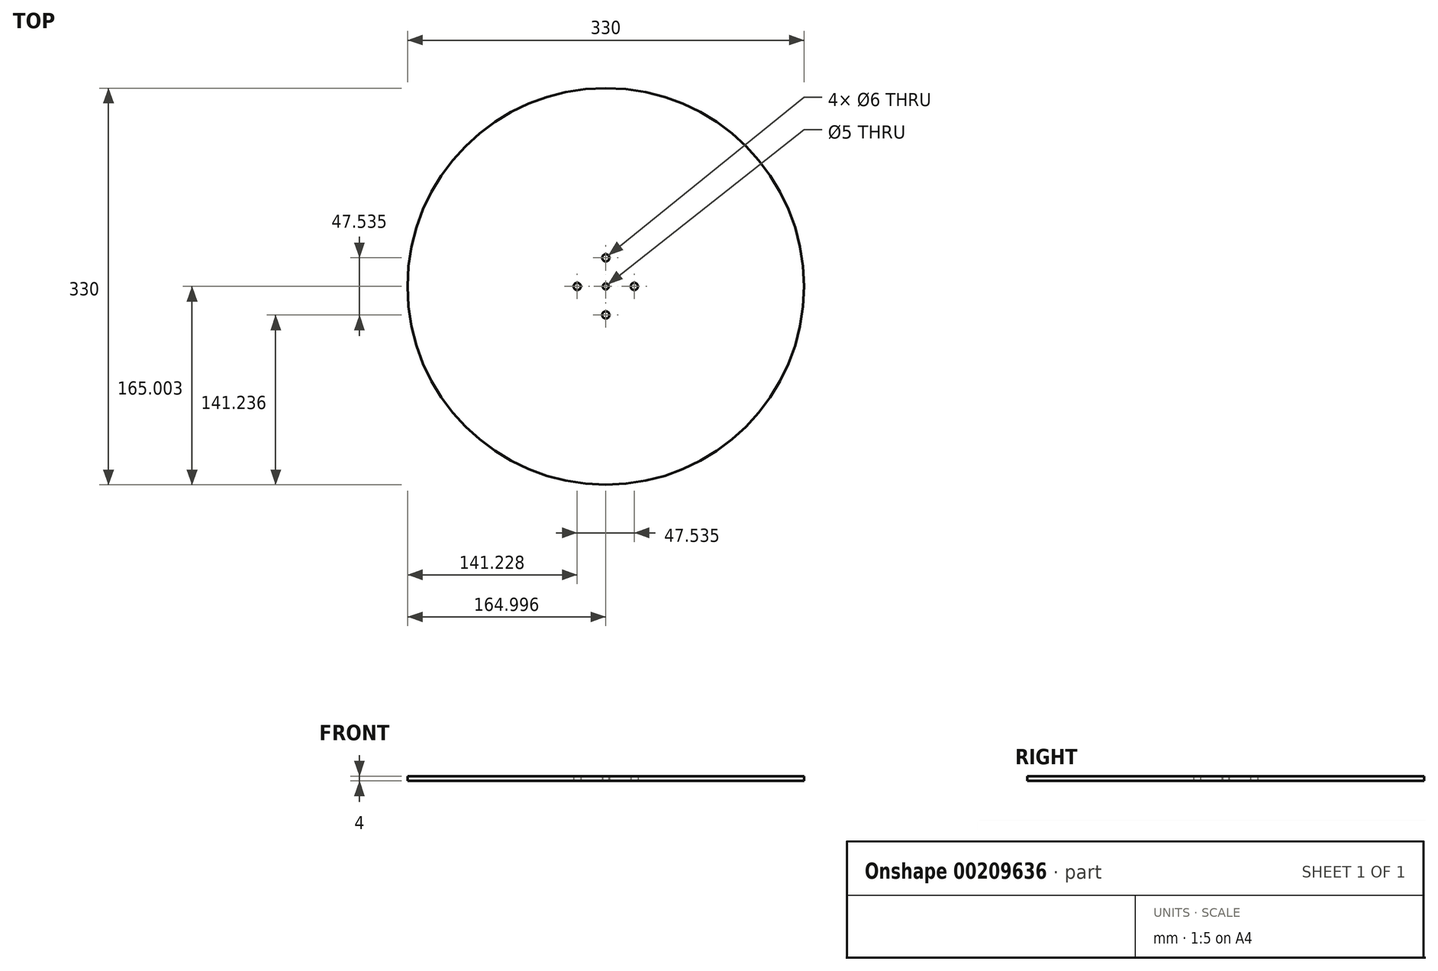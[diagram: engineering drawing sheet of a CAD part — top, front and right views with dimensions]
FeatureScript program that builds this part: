
annotation { "Feature Type Name" : "Feature", "Feature Type Description" : "" }
export const myFeature = defineFeature(function(context is Context, id is Id, definition is map)
    precondition{}
    {
        {
            var Q0;
            Q0=qCreatedBy(makeId("Top.planeOp"),FACE);
            var sketch = newSketch(context, id + "F0", { "sketchPlane" : qUnion([Q0])});
            skCircle(sketch, "E0", {"center": v(140.1, 209.35) * mm, "radius": 2.5 * mm});
            skCircle(sketch, "E1", {"center": v(140.1, 209.35) * mm, "radius": 165 * mm});
            skCircle(sketch, "E2", {"center": v(140.1, 209.35) * mm, "radius": 23.77 * mm, "construction": true});
            skCircle(sketch, "E3", {"center": v(140.1, 233.12) * mm, "radius": 3 * mm});
            skCircle(sketch, "E4", {"center": v(163.86, 209.35) * mm, "radius": 3 * mm});
            skCircle(sketch, "E5", {"center": v(116.33, 209.35) * mm, "radius": 3 * mm});
            skCircle(sketch, "E6", {"center": v(140.1, 185.59) * mm, "radius": 3 * mm});
            skSolve(sketch);
        }
        {
            var Q0;
            Q0=makeQuery(id+"F0.imprint","IMPRINT",FACE,{"disambiguationData":[TD([[makeQuery(id+"F0.imprint","IMPRINT",EDGE,{"derivedFrom":sQuery(id+"F0.wireOp",EDGE,"E0")}),-1.0]])]});
            extrude(context, id + "F1", {"entities" : qUnion([Q0]), "depth" : 4 * mm});
        }
    });
